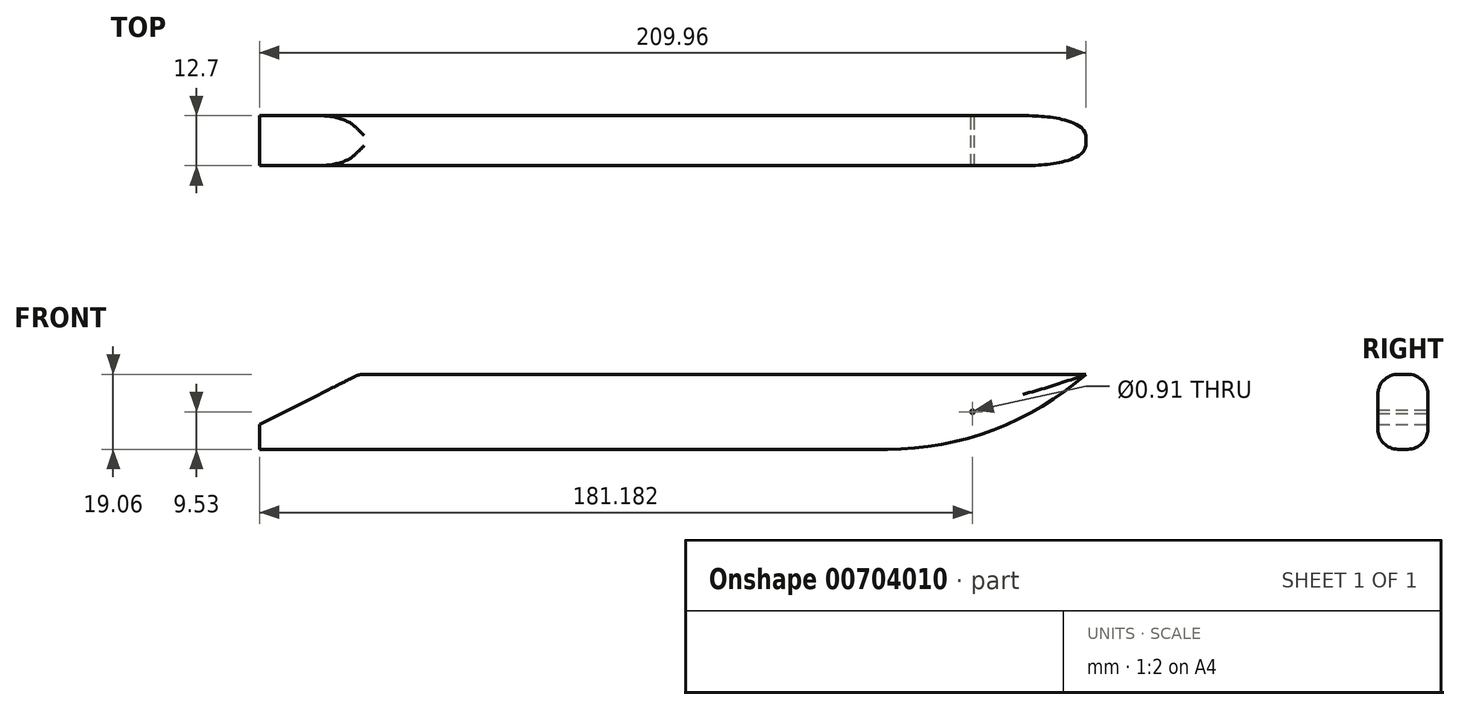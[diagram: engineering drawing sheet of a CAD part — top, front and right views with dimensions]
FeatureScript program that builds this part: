
annotation { "Feature Type Name" : "Feature", "Feature Type Description" : "" }
export const myFeature = defineFeature(function(context is Context, id is Id, definition is map)
    precondition{}
    {
        {
            var Q0;
            Q0=qCreatedBy(makeId("Front.planeOp"),FACE);
            var sketch = newSketch(context, id + "F0", { "sketchPlane" : qUnion([Q0])});
            skLineSegment(sketch, "E0.bottom", {"start": v(-104.98, 9.53) * mm, "end": v(104.98, 9.53) * mm});
            skLineSegment(sketch, "E0.top", {"start": v(-104.98, -9.53) * mm, "end": v(104.98, -9.53) * mm});
            skLineSegment(sketch, "E0.left", {"start": v(-104.98, 9.53) * mm, "end": v(-104.98, -9.53) * mm});
            skLineSegment(sketch, "E0.right", {"start": v(104.98, 9.53) * mm, "end": v(104.98, -9.53) * mm});
            skPoint(sketch, "E0.middle", {"position": v(0, 0) * mm});
            skCircle(sketch, "E1", {"center": v(76.2, 0) * mm, "radius": 0.46 * mm});
            skSolve(sketch);
        }
        {
            var Q0;
            Q0=makeQuery(id+"F0.imprint","IMPRINT",FACE,{"disambiguationData":[TD([[makeQuery(id+"F0.imprint","IMPRINT",EDGE,{"derivedFrom":sQuery(id+"F0.wireOp",EDGE,"E0.bottom")}),-1.0]])]});
            extrude(context, id + "F1", {"entities" : qUnion([Q0]), "depth" : 12.7 * mm, "offsetDistance" : 25.4 * mm});
        }
        {
            var Q0;
            Q0=makeQuery(id+"F1.opExtrude","SWEPT_EDGE",EDGE,{"disambiguationData":[OSD([sQuery(id+"F0.wireOp",EDGE,"E0.top"),sQuery(id+"F0.wireOp",EDGE,"E0.right")])]});
            fillet(context, id + "F2", {"entities" : qUnion([Q0]), "radius" : 76.2 * mm, "tangentPropagation" : true, "allowEdgeOverflow" : false});
        }
        {
            var Q0;
            Q0=makeQuery(id+"F1.opExtrude","SWEPT_EDGE",EDGE,{"disambiguationData":[OSD([sQuery(id+"F0.wireOp",EDGE,"E0.bottom"),sQuery(id+"F0.wireOp",EDGE,"E0.left")])]});
            chamfer(context, id + "F3", {"entities" : qUnion([Q0]), "chamferType" : ChamferType.TWO_OFFSETS, "width1" : 12.7 * mm, "oppositeDirection" : false, "width2" : 25.4 * mm, "tangentPropagation" : true});
        }
        {
            var Q0;
            {var subQ0=sQuery(id+"F0.wireOp",EDGE,"E0.right");var subQ1=sQuery(id+"F0.wireOp",EDGE,"E0.top");Q0=makeQuery(id+"F2.opFillet","BLEND_EDGE",EDGE,{"blendedFrom":[makeQuery(id+"F1.opExtrude","SWEPT_EDGE",EDGE,{"disambiguationData":[OSD([subQ1,subQ0])]}),makeQuery(id+"F1.opExtrude","CAP_FACE",FACE,{"disambiguationData":[OSD([sQuery(id+"F0.wireOp",EDGE,"E0.bottom"),subQ1,sQuery(id+"F0.wireOp",EDGE,"E0.left"),subQ0,sQuery(id+"F0.wireOp",EDGE,"E1")])],"isStart":false})],"blendedInto":[makeQuery(id+"F1.opExtrude","CAP_FACE",FACE,{"disambiguationData":[OSD([sQuery(id+"F0.wireOp",EDGE,"E0.bottom"),subQ1,sQuery(id+"F0.wireOp",EDGE,"E0.left"),subQ0,sQuery(id+"F0.wireOp",EDGE,"E1")])],"isStart":false})]});}
            var Q1;
            Q1=makeQuery(id+"F1.opExtrude","CAP_EDGE",EDGE,{"disambiguationData":[OSD([sQuery(id+"F0.wireOp",EDGE,"E0.bottom")])],"isStart":false});
            var Q2;
            Q2=makeQuery(id+"F1.opExtrude","CAP_EDGE",EDGE,{"disambiguationData":[OSD([sQuery(id+"F0.wireOp",EDGE,"E0.bottom")])],"isStart":true});
            var Q3;
            Q3=makeQuery(id+"F1.opExtrude","CAP_EDGE",EDGE,{"disambiguationData":[OSD([sQuery(id+"F0.wireOp",EDGE,"E0.top")])],"isStart":true});
            var Q4;
            {var subQ0=sQuery(id+"F0.wireOp",EDGE,"E0.bottom");Q4=makeQuery(id+"F3.opChamfer","BLEND_EDGE",EDGE,{"blendedFrom":[makeQuery(id+"F1.opExtrude","SWEPT_EDGE",EDGE,{"disambiguationData":[OSD([subQ0,sQuery(id+"F0.wireOp",EDGE,"E0.left")])]}),makeQuery(id+"F1.opExtrude","SWEPT_FACE",FACE,{"disambiguationData":[OSD([subQ0])]})],"blendedInto":[makeQuery(id+"F1.opExtrude","SWEPT_FACE",FACE,{"disambiguationData":[OSD([subQ0])]})]});}
            var Q5;
            Q5=makeQuery(id+"F1.opExtrude","CAP_EDGE",EDGE,{"disambiguationData":[OSD([sQuery(id+"F0.wireOp",EDGE,"E0.top")])],"isStart":false});
            var Q6;
            {var subQ0=sQuery(id+"F0.wireOp",EDGE,"E0.right");var subQ1=sQuery(id+"F0.wireOp",EDGE,"E0.top");Q6=makeQuery(id+"F2.opFillet","BLEND_EDGE",EDGE,{"blendedFrom":[makeQuery(id+"F1.opExtrude","SWEPT_EDGE",EDGE,{"disambiguationData":[OSD([subQ1,subQ0])]}),makeQuery(id+"F1.opExtrude","CAP_FACE",FACE,{"disambiguationData":[OSD([sQuery(id+"F0.wireOp",EDGE,"E0.bottom"),subQ1,sQuery(id+"F0.wireOp",EDGE,"E0.left"),subQ0,sQuery(id+"F0.wireOp",EDGE,"E1")])],"isStart":true})],"blendedInto":[makeQuery(id+"F1.opExtrude","CAP_FACE",FACE,{"disambiguationData":[OSD([sQuery(id+"F0.wireOp",EDGE,"E0.bottom"),subQ1,sQuery(id+"F0.wireOp",EDGE,"E0.left"),subQ0,sQuery(id+"F0.wireOp",EDGE,"E1")])],"isStart":true})]});}
            fillet(context, id + "F4", {"entities" : qUnion([Q0, Q1, Q2, Q3, Q4, Q5, Q6]), "radius" : 5.08 * mm, "tangentPropagation" : true, "allowEdgeOverflow" : false});
        }
    });
